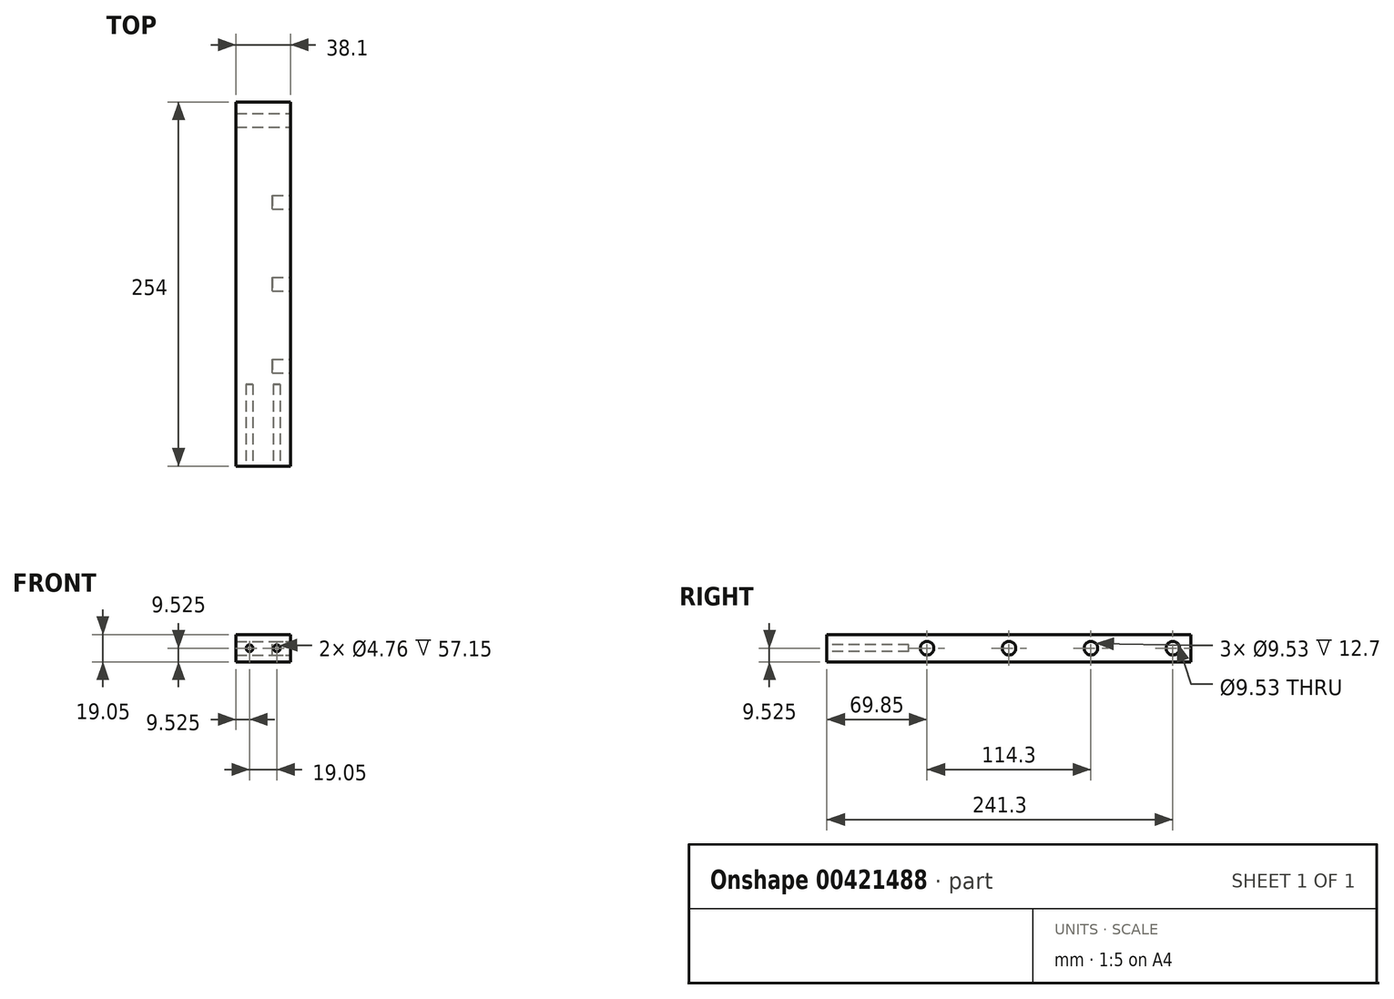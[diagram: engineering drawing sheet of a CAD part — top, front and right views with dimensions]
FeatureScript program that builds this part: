
annotation { "Feature Type Name" : "Feature", "Feature Type Description" : "" }
export const myFeature = defineFeature(function(context is Context, id is Id, definition is map)
    precondition{}
    {
        {
            var Q0;
            Q0=qCreatedBy(makeId("Top.planeOp"),FACE);
            var sketch = newSketch(context, id + "F0", { "sketchPlane" : qUnion([Q0])});
            skLineSegment(sketch, "E0.bottom", {"start": v(19.05, 127) * mm, "end": v(12.7, 127) * mm});
            skLineSegment(sketch, "E0.top", {"start": v(19.05, -127) * mm, "end": v(-19.05, -127) * mm});
            skLineSegment(sketch, "E0.left", {"start": v(19.05, 127) * mm, "end": v(19.05, -127) * mm});
            skLineSegment(sketch, "E0.right", {"start": v(-19.05, 63.5) * mm, "end": v(-19.05, -127) * mm});
            skPoint(sketch, "E0.middle", {"position": v(0, 0) * mm});
            skLineSegment(sketch, "E1", {"start": v(-19.05, 63.5) * mm, "end": v(12.7, 127) * mm});
            skPoint(sketch, "E2.orphan", {"position": v(-19.05, 127) * mm});
            skLineSegment(sketch, "E3", {"start": v(12.7, 127) * mm, "end": v(-19.05, 127) * mm});
            skLineSegment(sketch, "E4", {"start": v(-19.05, 127) * mm, "end": v(-19.05, 63.5) * mm});
            skSolve(sketch);
        }
        {
            var Q0;
            Q0 = qSketchRegion(id + "F0", true);
            extrude(context, id + "F1", {"entities" : qUnion([Q0]), "depth" : 19.05 * mm});
        }
        {
            var Q0;
            Q0=makeQuery(id+"F1.opExtrude","SWEPT_FACE",FACE,{"disambiguationData":[OSD([sQuery(id+"F0.wireOp",EDGE,"E0.left")])]});
            var sketch = newSketch(context, id + "F2", { "sketchPlane" : qUnion([Q0])});
            skLineSegment(sketch, "E5", {"start": v(127, 9.53) * mm, "end": v(-127, 9.53) * mm, "construction": true});
            skCircle(sketch, "E6", {"center": v(114.3, 9.53) * mm, "radius": 4.76 * mm});
            skCircle(sketch, "E7", {"center": v(0, 9.53) * mm, "radius": 4.76 * mm});
            skCircle(sketch, "E8", {"center": v(-57.15, 9.53) * mm, "radius": 4.76 * mm});
            skCircle(sketch, "E9", {"center": v(57.15, 9.53) * mm, "radius": 4.76 * mm});
            skSolve(sketch);
        }
        {
            var Q0;
            Q0=makeQuery(id+"F2.imprint","IMPRINT",FACE,{"disambiguationData":[TD([[makeQuery(id+"F2.imprint","IMPRINT",EDGE,{"derivedFrom":sQuery(id+"F2.wireOp",EDGE,"E6")}),1.0]])]});
            var Q1;
            Q1=sQuery(id+"F2.wireOp",EDGE,"E6");
            extrude(context, id + "F3", {"entities" : qUnion([Q0]), "operationType" : NewBodyOperationType.REMOVE, "surfaceEntities" : qUnion([Q1]), "endBound" : BoundingType.THROUGH_ALL, "oppositeDirection" : true, "depth" : 25.4 * mm});
        }
        {
            var Q0;
            Q0=makeQuery(id+"F1.opExtrude","SWEPT_FACE",FACE,{"disambiguationData":[OSD([sQuery(id+"F0.wireOp",EDGE,"E0.top")])]});
            var sketch = newSketch(context, id + "F4", { "sketchPlane" : qUnion([Q0])});
            skLineSegment(sketch, "E10", {"start": v(-19.05, 9.53) * mm, "end": v(19.05, 9.53) * mm, "construction": true});
            skCircle(sketch, "E11", {"center": v(-9.52, 9.53) * mm, "radius": 2.38 * mm});
            skCircle(sketch, "E12", {"center": v(9.53, 9.53) * mm, "radius": 2.38 * mm});
            skSolve(sketch);
        }
        {
            var Q0;
            Q0 = qSketchRegion(id + "F4", true);
            extrude(context, id + "F5", {"entities" : qUnion([Q0]), "operationType" : NewBodyOperationType.REMOVE, "oppositeDirection" : true, "depth" : 57.15 * mm});
        }
        {
            var Q0;
            Q0=makeQuery(id+"F2.imprint","IMPRINT",FACE,{"disambiguationData":[TD([[makeQuery(id+"F2.imprint","IMPRINT",EDGE,{"derivedFrom":sQuery(id+"F2.wireOp",EDGE,"E8")}),1.0]])]});
            var Q1;
            Q1=makeQuery(id+"F2.imprint","IMPRINT",FACE,{"disambiguationData":[TD([[makeQuery(id+"F2.imprint","IMPRINT",EDGE,{"derivedFrom":sQuery(id+"F2.wireOp",EDGE,"E7")}),1.0]])]});
            var Q2;
            Q2=makeQuery(id+"F2.imprint","IMPRINT",FACE,{"disambiguationData":[TD([[makeQuery(id+"F2.imprint","IMPRINT",EDGE,{"derivedFrom":sQuery(id+"F2.wireOp",EDGE,"E9")}),1.0]])]});
            extrude(context, id + "F6", {"entities" : qUnion([Q0, Q1, Q2]), "operationType" : NewBodyOperationType.REMOVE, "oppositeDirection" : true, "depth" : 12.7 * mm});
        }
    });
